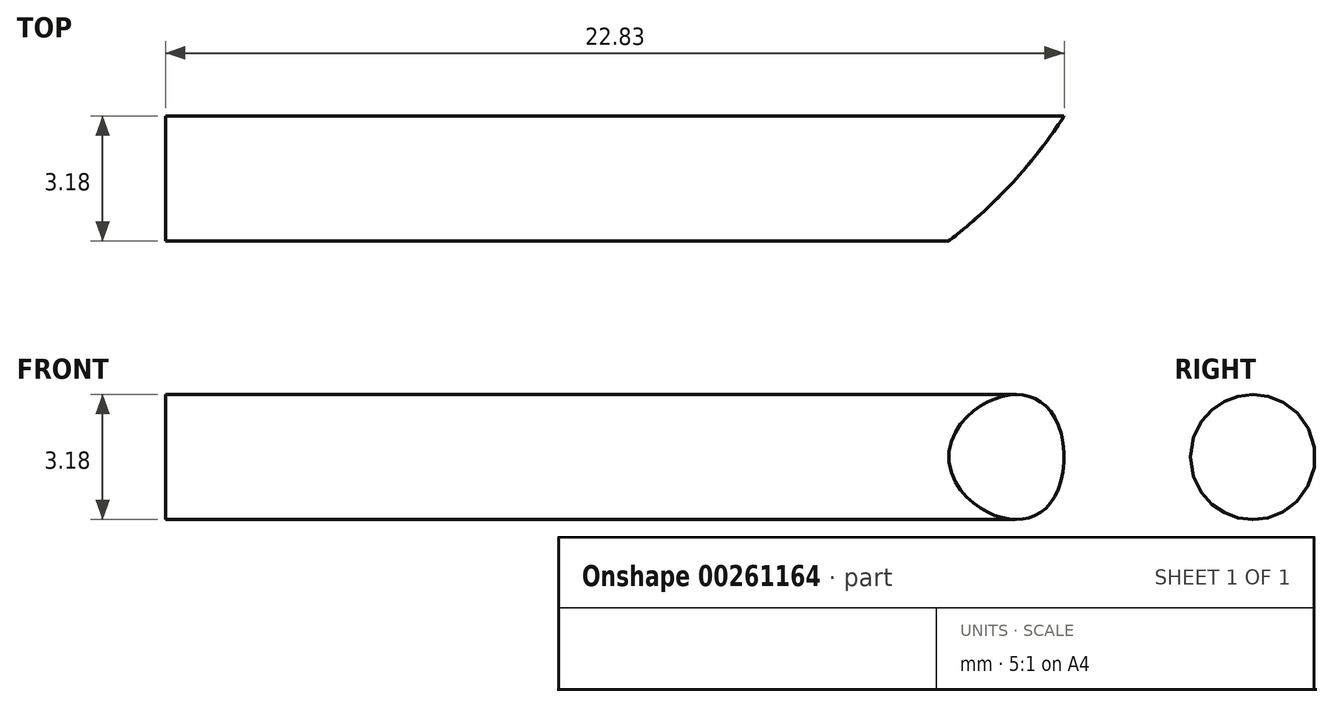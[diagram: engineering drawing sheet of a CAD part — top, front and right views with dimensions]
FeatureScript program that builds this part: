
annotation { "Feature Type Name" : "Feature", "Feature Type Description" : "" }
export const myFeature = defineFeature(function(context is Context, id is Id, definition is map)
    precondition{}
    {
        {
            var Q0;
            Q0=qCreatedBy(makeId("Right.planeOp"),FACE);
            var sketch = newSketch(context, id + "F0", { "sketchPlane" : qUnion([Q0])});
            skCircle(sketch, "E0", {"center": v(0, 0) * mm, "radius": 1.59 * mm});
            skSolve(sketch);
        }
        {
            var Q0;
            Q0 = qSketchRegion(id + "F0", true);
            extrude(context, id + "F1", {"entities" : qUnion([Q0]), "endBound" : BoundingType.SYMMETRIC, "depth" : 25.4 * mm});
        }
        {
            var Q0;
            Q0=makeQuery(id+"F1.opExtrude","CAP_FACE",FACE,{"disambiguationData":[OSD([sQuery(id+"F0.wireOp",EDGE,"E0")])],"isStart":true});
            var sketch = newSketch(context, id + "F2", { "sketchPlane" : qUnion([Q0])});
            skLineSegment(sketch, "E1.bottom", {"start": v(0, 1.59) * mm, "end": v(-4.19, 1.59) * mm});
            skLineSegment(sketch, "E1.top", {"start": v(0, -1.59) * mm, "end": v(-4.19, -1.59) * mm});
            skLineSegment(sketch, "E1.left", {"start": v(0, 1.59) * mm, "end": v(0, -1.59) * mm});
            skLineSegment(sketch, "E1.right", {"start": v(-4.19, 1.59) * mm, "end": v(-4.19, -1.59) * mm});
            skSolve(sketch);
        }
        {
            var Q0;
            Q0 = qSketchRegion(id + "F2", true);
            extrude(context, id + "F3", {"entities" : qUnion([Q0]), "operationType" : NewBodyOperationType.ADD, "depth" : 1.59 * mm});
        }
        {
            var Q0;
            Q0=makeQuery(id+"F3.opExtrude","SWEPT_FACE",FACE,{"disambiguationData":[OSD([sQuery(id+"F2.wireOp",EDGE,"E1.bottom")])]});
            var sketch = newSketch(context, id + "F4", { "sketchPlane" : qUnion([Q0])});
            skArc(sketch, "E2", {"start": v(7.72, -1.59) * mm, "mid": v(9.33, -0.13) * mm, "end": v(10.66, 1.59) * mm});
            skLineSegment(sketch, "E3", {"start": v(10.66, 1.59) * mm, "end": v(1.65, 1.59) * mm, "construction": true});
            skLineSegment(sketch, "E4", {"start": v(7.72, -1.59) * mm, "end": v(1.65, -1.59) * mm, "construction": true});
            skLineSegment(sketch, "E5", {"start": v(1.65, 1.59) * mm, "end": v(-8.44, 1.59) * mm, "construction": true});
            skLineSegment(sketch, "E6", {"start": v(10.66, 1.59) * mm, "end": v(12.7, 1.59) * mm});
            skLineSegment(sketch, "E7", {"start": v(12.7, 1.59) * mm, "end": v(12.7, -1.59) * mm});
            skLineSegment(sketch, "E8", {"start": v(12.7, -1.59) * mm, "end": v(7.72, -1.59) * mm});
            skLineSegment(sketch, "E9.bottom", {"start": v(-12.17, 1.59) * mm, "end": v(-15.82, 1.59) * mm});
            skLineSegment(sketch, "E9.top", {"start": v(-12.17, 5.26) * mm, "end": v(-15.82, 5.26) * mm});
            skLineSegment(sketch, "E9.left", {"start": v(-12.17, 1.59) * mm, "end": v(-12.17, 5.26) * mm});
            skLineSegment(sketch, "E9.right", {"start": v(-15.82, 1.59) * mm, "end": v(-15.82, 5.26) * mm});
            skLineSegment(sketch, "E10.top", {"start": v(-12.17, -3.5) * mm, "end": v(-15.82, -3.5) * mm});
            skLineSegment(sketch, "E10.left", {"start": v(-12.17, 1.59) * mm, "end": v(-12.17, -3.5) * mm});
            skLineSegment(sketch, "E10.right", {"start": v(-15.82, 1.59) * mm, "end": v(-15.82, -3.5) * mm});
            skSolve(sketch);
        }
        {
            var Q0;
            Q0 = qSketchRegion(id + "F4", true);
            extrude(context, id + "F5", {"entities" : qUnion([Q0]), "operationType" : NewBodyOperationType.REMOVE, "oppositeDirection" : true, "depth" : 25.4 * mm});
        }
    });
